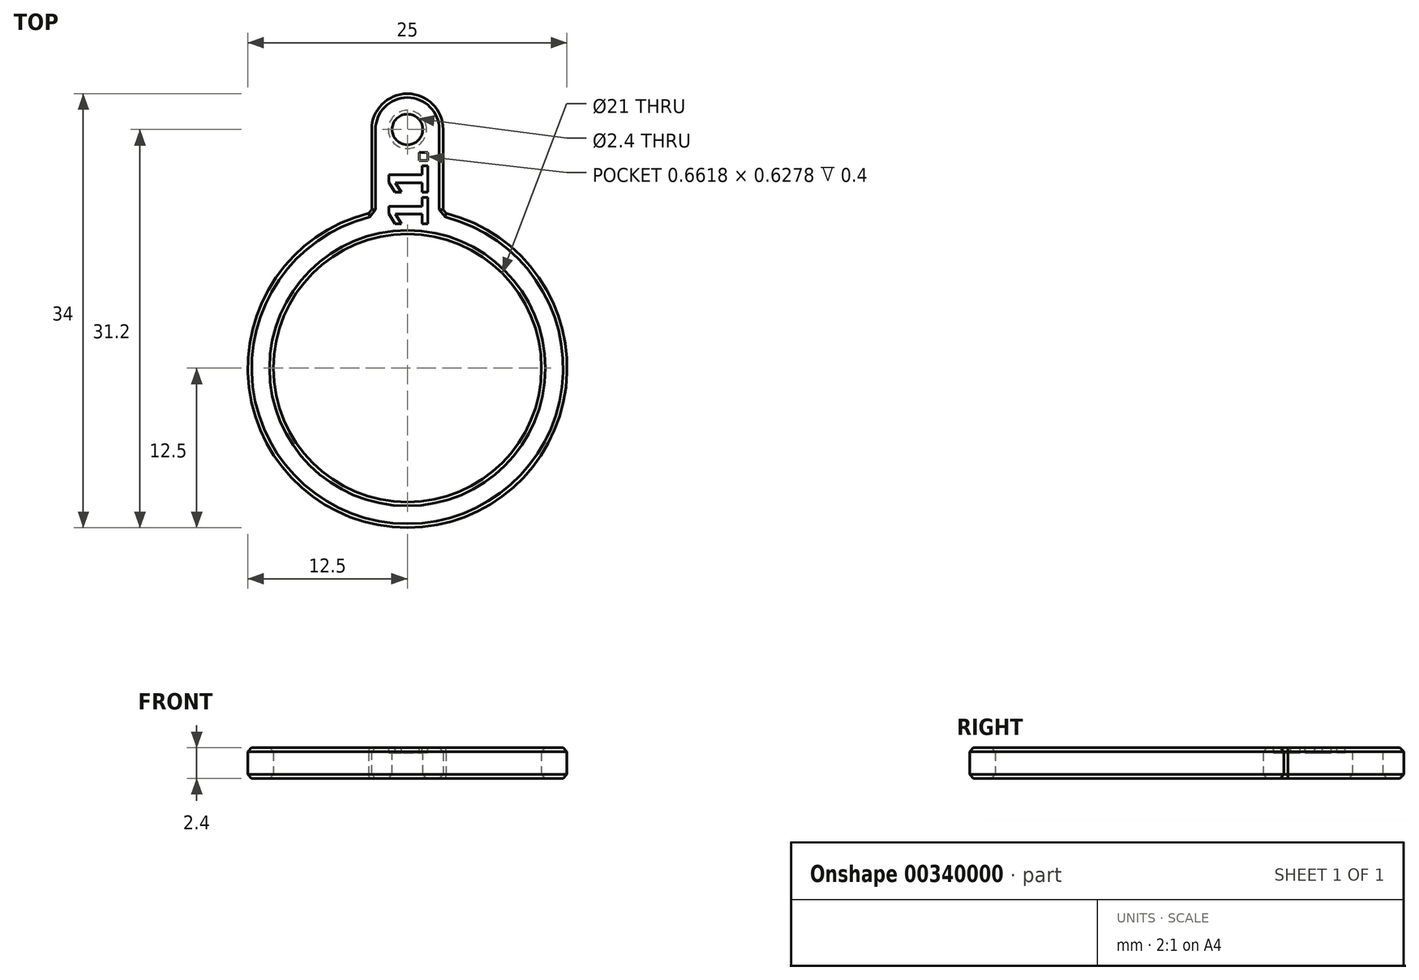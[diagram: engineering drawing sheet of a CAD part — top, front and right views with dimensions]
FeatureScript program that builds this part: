
annotation { "Feature Type Name" : "Feature", "Feature Type Description" : "" }
export const myFeature = defineFeature(function(context is Context, id is Id, definition is map)
    precondition{}
    {
        {
            var Q0;
            Q0=qCreatedBy(makeId("Top.planeOp"),FACE);
            var sketch = newSketch(context, id + "F0", { "sketchPlane" : qUnion([Q0])});
            skCircle(sketch, "E0", {"center": v(0, 0) * mm, "radius": 10.5 * mm});
            skCircle(sketch, "E1", {"center": v(0, 0) * mm, "radius": 12.5 * mm});
            skLineSegment(sketch, "E2.bottom", {"start": v(2.8, 3.5) * mm, "end": v(-2.8, 3.5) * mm});
            skLineSegment(sketch, "E2.top", {"start": v(2.8, 21.5) * mm, "end": v(-2.8, 21.5) * mm});
            skLineSegment(sketch, "E2.left", {"start": v(2.8, 3.5) * mm, "end": v(2.8, 21.5) * mm});
            skLineSegment(sketch, "E2.right", {"start": v(-2.8, 3.5) * mm, "end": v(-2.8, 21.5) * mm});
            skPoint(sketch, "E2.middle", {"position": v(0, 12.5) * mm});
            skSolve(sketch);
        }
        {
            var Q0;
            Q0=qSketchRegion(id+"F0",true);
            extrude(context, id + "F1", {"entities" : qUnion([Q0]), "depth" : 2.4 * mm});
        }
        {
            var Q0;
            Q0=makeQuery(id+"F1.opExtrude","SWEPT_EDGE",EDGE,{"disambiguationData":[OSD([sQuery(id+"F0.wireOp",EDGE,"E2.top"),sQuery(id+"F0.wireOp",EDGE,"E2.right")])]});
            var Q1;
            Q1=makeQuery(id+"F1.opExtrude","SWEPT_EDGE",EDGE,{"disambiguationData":[OSD([sQuery(id+"F0.wireOp",EDGE,"E2.top"),sQuery(id+"F0.wireOp",EDGE,"E2.left")])]});
            fillet(context, id + "F2", {"entities" : qUnion([Q0, Q1]), "radius" : 2.8 * mm, "tangentPropagation" : true, "allowEdgeOverflow" : false});
        }
        {
            var Q0;
            Q0=makeQuery(id+"F1.opExtrude","CAP_FACE",FACE,{"disambiguationData":[OSD([sQuery(id+"F0.wireOp",EDGE,"E0"),sQuery(id+"F0.wireOp",EDGE,"E1"),sQuery(id+"F0.wireOp",EDGE,"E2.top"),sQuery(id+"F0.wireOp",EDGE,"E2.left"),sQuery(id+"F0.wireOp",EDGE,"E2.right")])],"isStart":false});
            var sketch = newSketch(context, id + "F3", { "sketchPlane" : qUnion([Q0])});
            skCircle(sketch, "E3", {"center": v(0, 18.7) * mm, "radius": 1.2 * mm});
            skSolve(sketch);
        }
        {
            var Q0;
            Q0=qSketchRegion(id+"F3",true);
            extrude(context, id + "F4", {"entities" : qUnion([Q0]), "operationType" : NewBodyOperationType.REMOVE, "oppositeDirection" : true, "depth" : 25 * mm});
        }
        {
            var Q0;
            Q0=makeQuery(id+"F4.boolean.opBoolean","COPY",EDGE,{"derivedFrom":makeQuery(id+"F4.opExtrude","CAP_EDGE",EDGE,{"disambiguationData":[OSD([sQuery(id+"F3.wireOp",EDGE,"E3")])],"isStart":true})});
            var Q1;
            Q1=makeQuery(id+"F4.boolean.opBoolean","INTERSECT",EDGE,{"derivedFrom":[makeQuery(id+"F1.opExtrude","CAP_FACE",FACE,{"disambiguationData":[OSD([sQuery(id+"F0.wireOp",EDGE,"E0"),sQuery(id+"F0.wireOp",EDGE,"E1"),sQuery(id+"F0.wireOp",EDGE,"E2.top"),sQuery(id+"F0.wireOp",EDGE,"E2.left"),sQuery(id+"F0.wireOp",EDGE,"E2.right")])],"isStart":true}),makeQuery(id+"F4.opExtrude","SWEPT_FACE",FACE,{"disambiguationData":[OSD([sQuery(id+"F3.wireOp",EDGE,"E3")])]})]});
            var Q2;
            {var subQ0=sQuery(id+"F0.wireOp",EDGE,"E2.right");var subQ1=sQuery(id+"F0.wireOp",EDGE,"E2.top");Q2=makeQuery(id+"F2.opFillet","BLEND_EDGE",EDGE,{"blendedFrom":[makeQuery(id+"F1.opExtrude","SWEPT_EDGE",EDGE,{"disambiguationData":[OSD([subQ1,subQ0])]}),makeQuery(id+"F1.opExtrude","CAP_FACE",FACE,{"disambiguationData":[OSD([sQuery(id+"F0.wireOp",EDGE,"E0"),sQuery(id+"F0.wireOp",EDGE,"E1"),subQ1,sQuery(id+"F0.wireOp",EDGE,"E2.left"),subQ0])],"isStart":true})],"blendedInto":[makeQuery(id+"F1.opExtrude","CAP_FACE",FACE,{"disambiguationData":[OSD([sQuery(id+"F0.wireOp",EDGE,"E0"),sQuery(id+"F0.wireOp",EDGE,"E1"),subQ1,sQuery(id+"F0.wireOp",EDGE,"E2.left"),subQ0])],"isStart":true})]});}
            var Q3;
            {var subQ0=sQuery(id+"F0.wireOp",EDGE,"E2.right");var subQ1=sQuery(id+"F0.wireOp",EDGE,"E2.top");Q3=makeQuery(id+"F2.opFillet","BLEND_EDGE",EDGE,{"blendedFrom":[makeQuery(id+"F1.opExtrude","SWEPT_EDGE",EDGE,{"disambiguationData":[OSD([subQ1,subQ0])]}),makeQuery(id+"F1.opExtrude","CAP_FACE",FACE,{"disambiguationData":[OSD([sQuery(id+"F0.wireOp",EDGE,"E0"),sQuery(id+"F0.wireOp",EDGE,"E1"),subQ1,sQuery(id+"F0.wireOp",EDGE,"E2.left"),subQ0])],"isStart":false})],"blendedInto":[makeQuery(id+"F1.opExtrude","CAP_FACE",FACE,{"disambiguationData":[OSD([sQuery(id+"F0.wireOp",EDGE,"E0"),sQuery(id+"F0.wireOp",EDGE,"E1"),subQ1,sQuery(id+"F0.wireOp",EDGE,"E2.left"),subQ0])],"isStart":false})]});}
            var Q4;
            Q4=makeQuery(id+"F1.opExtrude","CAP_EDGE",EDGE,{"disambiguationData":[OSD([sQuery(id+"F0.wireOp",EDGE,"E1")])],"isStart":false});
            var Q5;
            Q5=makeQuery(id+"F1.opExtrude","CAP_EDGE",EDGE,{"disambiguationData":[OSD([sQuery(id+"F0.wireOp",EDGE,"E1")])],"isStart":true});
            var Q6;
            Q6=makeQuery(id+"F1.opExtrude","SWEPT_EDGE",EDGE,{"disambiguationData":[OSD([sQuery(id+"F0.wireOp",EDGE,"E1"),sQuery(id+"F0.wireOp",EDGE,"E2.left")])]});
            var Q7;
            Q7=makeQuery(id+"F1.opExtrude","SWEPT_EDGE",EDGE,{"disambiguationData":[OSD([sQuery(id+"F0.wireOp",EDGE,"E1"),sQuery(id+"F0.wireOp",EDGE,"E2.right")])]});
            var Q8;
            Q8=makeQuery(id+"F1.opExtrude","CAP_EDGE",EDGE,{"disambiguationData":[OSD([sQuery(id+"F0.wireOp",EDGE,"E0")])],"isStart":true});
            var Q9;
            Q9=makeQuery(id+"F1.opExtrude","CAP_EDGE",EDGE,{"disambiguationData":[OSD([sQuery(id+"F0.wireOp",EDGE,"E0")])],"isStart":false});
            chamfer(context, id + "F5", {"entities" : qUnion([Q0, Q1, Q2, Q3, Q4, Q5, Q6, Q7, Q8, Q9]), "width" : 0.3 * mm, "tangentPropagation" : true});
        }
        {
            var Q0;
            Q0=makeQuery(id+"F1.opExtrude","CAP_FACE",FACE,{"disambiguationData":[OSD([sQuery(id+"F0.wireOp",EDGE,"E0"),sQuery(id+"F0.wireOp",EDGE,"E1"),sQuery(id+"F0.wireOp",EDGE,"E2.top"),sQuery(id+"F0.wireOp",EDGE,"E2.left"),sQuery(id+"F0.wireOp",EDGE,"E2.right")])],"isStart":false});
            var sketch = newSketch(context, id + "F6", { "sketchPlane" : qUnion([Q0])});
            skText(sketch, "E4", { "text": "11.\n", "fontName": "Arimo-Bold.ttf"});
            skLineSegment(sketch, "E5", {"start": v(0, 11.02) * mm, "end": v(0, 0) * mm});
            skPoint(sketch, "E5.endSnap0", {"position": v(0, 11.02) * mm});
            const initialGuessF6  = {"E4": [0.0016, 0.01102, 0, 1, 0.0032]};
            skSetInitialGuess(sketch, initialGuessF6);
            skSolve(sketch);
        }
        {
            var Q0;
            Q0=qSketchRegion(id+"F6",true);
            extrude(context, id + "F7", {"entities" : qUnion([Q0]), "operationType" : NewBodyOperationType.REMOVE, "oppositeDirection" : true, "depth" : 0.4 * mm});
        }
    });
